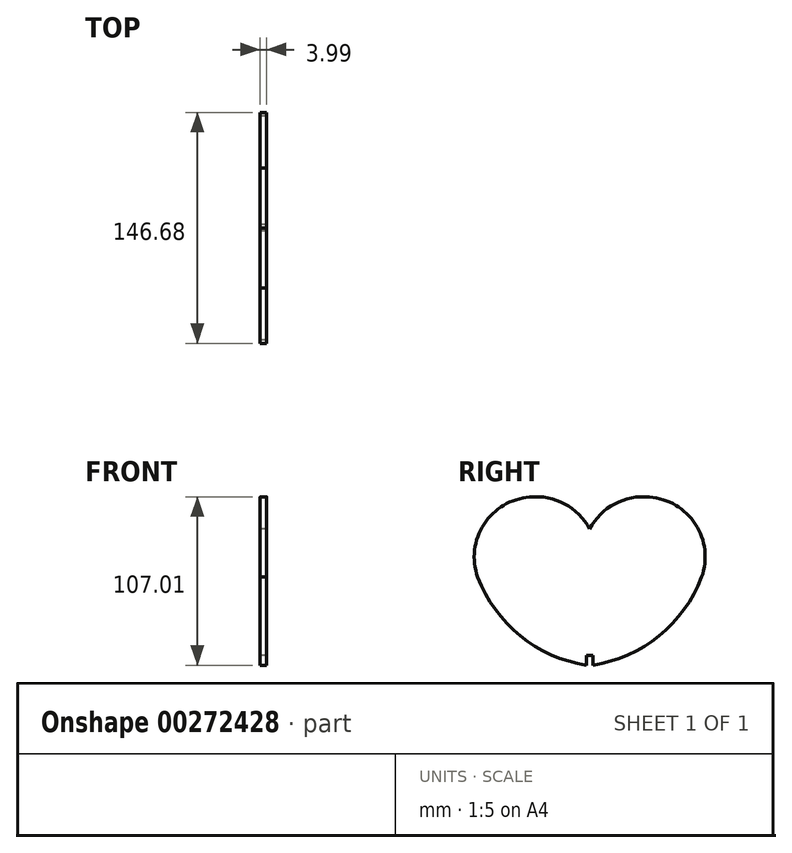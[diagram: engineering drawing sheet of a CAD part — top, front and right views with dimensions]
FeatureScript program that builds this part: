
annotation { "Feature Type Name" : "Feature", "Feature Type Description" : "" }
export const myFeature = defineFeature(function(context is Context, id is Id, definition is map)
    precondition{}
    {
        {
            var Q0;
            Q0=qCreatedBy(makeId("Right.planeOp"),FACE);
            var sketch = newSketch(context, id + "F0", { "sketchPlane" : qUnion([Q0])});
            skLineSegment(sketch, "E0", {"start": v(0, 0) * mm, "end": v(0, -49.62) * mm});
            skLineSegment(sketch, "E1", {"start": v(0, 0) * mm, "end": v(0, 30.48) * mm});
            skArc(sketch, "E2", {"start": v(-71.12, 0) * mm, "mid": v(-44.06, -37.25) * mm, "end": v(-2, -55.97) * mm});
            skArc(sketch, "E3", {"start": v(-38.1, 50.8) * mm, "mid": v(-67.18, 33.57) * mm, "end": v(-71.12, 0) * mm});
            skArc(sketch, "E4", {"start": v(0, 30.48) * mm, "mid": v(-15.9, 46.56) * mm, "end": v(-38.1, 50.8) * mm});
            skArc(sketch, "E5", {"start": v(38.1, 50.8) * mm, "mid": v(15.9, 46.56) * mm, "end": v(0, 30.48) * mm});
            skArc(sketch, "E6", {"start": v(71.12, 0) * mm, "mid": v(67.18, 33.57) * mm, "end": v(38.1, 50.8) * mm});
            skArc(sketch, "E7", {"start": v(2, -55.97) * mm, "mid": v(44.06, -37.25) * mm, "end": v(71.12, 0) * mm});
            skLineSegment(sketch, "E8", {"start": v(-2, -55.97) * mm, "end": v(-2, -49.62) * mm});
            skLineSegment(sketch, "E9", {"start": v(-2, -49.62) * mm, "end": v(2, -49.62) * mm});
            skLineSegment(sketch, "E10", {"start": v(2, -49.62) * mm, "end": v(2, -55.97) * mm});
            skPoint(sketch, "E11.orphan", {"position": v(0, -56.26) * mm});
            skSolve(sketch);
        }
        {
            var Q0;
            Q0 = qSketchRegion(id + "F0", true);
            extrude(context, id + "F1", {"entities" : qUnion([Q0]), "depth" : 4 * mm});
        }
    });
